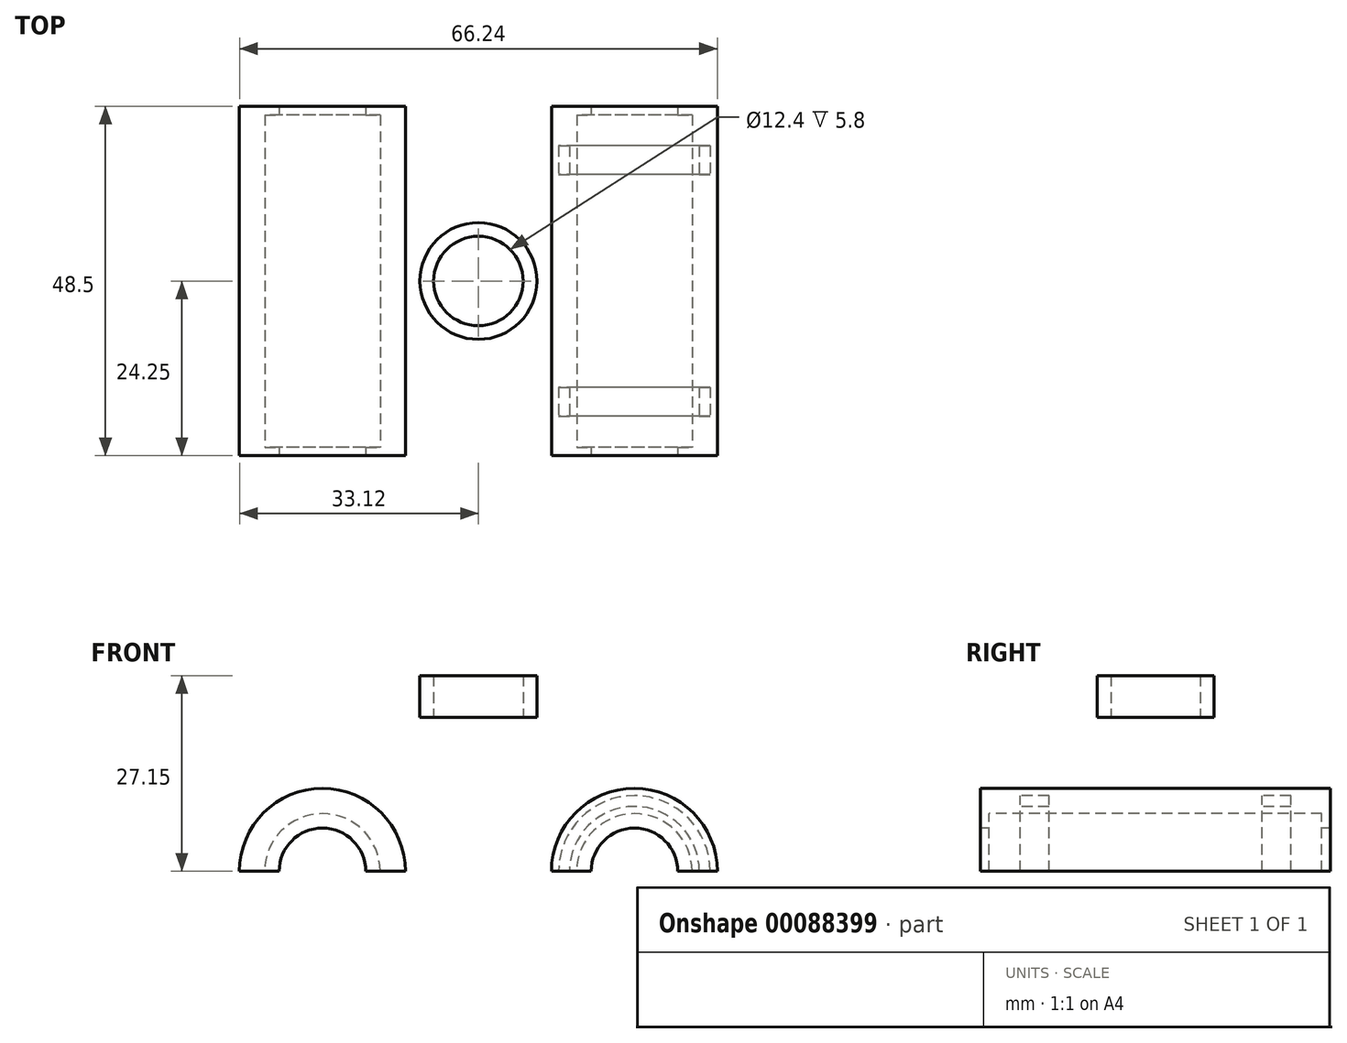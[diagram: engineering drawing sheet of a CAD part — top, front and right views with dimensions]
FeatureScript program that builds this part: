
annotation { "Feature Type Name" : "Feature", "Feature Type Description" : "" }
export const myFeature = defineFeature(function(context is Context, id is Id, definition is map)
    precondition{}
    {
        {
            var Q0;
            Q0=qCreatedBy(makeId("Front.planeOp"),FACE);
            var sketch = newSketch(context, id + "F0", { "sketchPlane" : qUnion([Q0])});
            skLineSegment(sketch, "E0", {"start": v(-21.63, 0) * mm, "end": v(21.63, 0) * mm, "construction": true});
            skCircle(sketch, "E1", {"center": v(-21.63, 0) * mm, "radius": 8 * mm});
            skCircle(sketch, "E2", {"center": v(21.63, 0) * mm, "radius": 8 * mm});
            skCircle(sketch, "E3", {"center": v(-21.63, 0) * mm, "radius": 6 * mm});
            skCircle(sketch, "E4", {"center": v(21.63, 0) * mm, "radius": 6 * mm});
            skCircle(sketch, "E5", {"center": v(-21.63, 0) * mm, "radius": 11.5 * mm});
            skCircle(sketch, "E6", {"center": v(21.63, 0) * mm, "radius": 11.5 * mm});
            skLineSegment(sketch, "E7", {"start": v(-33.12, 0) * mm, "end": v(33.12, 0) * mm});
            skSolve(sketch);
        }
        {
            var Q0;
            {var subQ0=sQuery(id+"F0.wireOp",EDGE,"E7");var subQ1=sQuery(id+"F0.wireOp",EDGE,"E1");var subQ2=makeQuery(id+"F0.imprint","INTERSECT",VERTEX,{"disambiguationData":[OD(0.0)],"derivedFrom":[subQ1,subQ0]});Q0=makeQuery(id+"F0.imprint","IMPRINT",FACE,{"disambiguationData":[TD([[makeQuery(id+"F0.imprint","IMPRINT",EDGE,{"disambiguationData":[TD([[subQ2,1.0]])],"derivedFrom":subQ1}),1.0]])]});}
            var Q1;
            {var subQ0=sQuery(id+"F0.wireOp",EDGE,"E7");var subQ1=sQuery(id+"F0.wireOp",EDGE,"E1");var subQ2=makeQuery(id+"F0.imprint","INTERSECT",VERTEX,{"disambiguationData":[OD(0.0)],"derivedFrom":[subQ1,subQ0]});Q1=makeQuery(id+"F0.imprint","IMPRINT",FACE,{"disambiguationData":[TD([[makeQuery(id+"F0.imprint","IMPRINT",EDGE,{"disambiguationData":[TD([[subQ2,1.0]])],"derivedFrom":subQ1}),-1.0]])]});}
            var Q2;
            {var subQ0=sQuery(id+"F0.wireOp",EDGE,"E7");var subQ1=sQuery(id+"F0.wireOp",EDGE,"E2");var subQ2=makeQuery(id+"F0.imprint","INTERSECT",VERTEX,{"disambiguationData":[OD(0.0)],"derivedFrom":[subQ1,subQ0]});Q2=makeQuery(id+"F0.imprint","IMPRINT",FACE,{"disambiguationData":[TD([[makeQuery(id+"F0.imprint","IMPRINT",EDGE,{"disambiguationData":[TD([[subQ2,1.0]])],"derivedFrom":subQ1}),1.0]])]});}
            var Q3;
            {var subQ0=sQuery(id+"F0.wireOp",EDGE,"E7");var subQ1=sQuery(id+"F0.wireOp",EDGE,"E2");var subQ2=makeQuery(id+"F0.imprint","INTERSECT",VERTEX,{"disambiguationData":[OD(0.0)],"derivedFrom":[subQ1,subQ0]});Q3=makeQuery(id+"F0.imprint","IMPRINT",FACE,{"disambiguationData":[TD([[makeQuery(id+"F0.imprint","IMPRINT",EDGE,{"disambiguationData":[TD([[subQ2,1.0]])],"derivedFrom":subQ1}),-1.0]])]});}
            extrude(context, id + "F1", {"entities" : qUnion([Q0, Q1, Q2, Q3]), "oppositeDirection" : true, "depth" : 48.5 * mm});
        }
        {
            var Q0;
            {var subQ0=sQuery(id+"F0.wireOp",EDGE,"E7");var subQ1=sQuery(id+"F0.wireOp",EDGE,"E1");var subQ2=makeQuery(id+"F0.imprint","INTERSECT",VERTEX,{"disambiguationData":[OD(0.0)],"derivedFrom":[subQ1,subQ0]});Q0=makeQuery(id+"F0.imprint","IMPRINT",FACE,{"disambiguationData":[TD([[makeQuery(id+"F0.imprint","IMPRINT",EDGE,{"disambiguationData":[TD([[subQ2,1.0]])],"derivedFrom":subQ1}),1.0]])]});}
            var Q1;
            {var subQ0=sQuery(id+"F0.wireOp",EDGE,"E7");var subQ1=sQuery(id+"F0.wireOp",EDGE,"E2");var subQ2=makeQuery(id+"F0.imprint","INTERSECT",VERTEX,{"disambiguationData":[OD(0.0)],"derivedFrom":[subQ1,subQ0]});Q1=makeQuery(id+"F0.imprint","IMPRINT",FACE,{"disambiguationData":[TD([[makeQuery(id+"F0.imprint","IMPRINT",EDGE,{"disambiguationData":[TD([[subQ2,1.0]])],"derivedFrom":subQ1}),1.0]])]});}
            extrude(context, id + "F2", {"entities" : qUnion([Q0, Q1]), "operationType" : NewBodyOperationType.REMOVE, "oppositeDirection" : true, "depth" : 47.3 * mm, "hasSecondDirection" : true, "secondDirectionOppositeDirection" : true, "secondDirectionDepth" : 1.2 * mm});
        }
        {
            var Q0;
            Q0=qCreatedBy(makeId("Front.planeOp"),FACE);
            var sketch = newSketch(context, id + "F3", { "sketchPlane" : qUnion([Q0])});
            skPoint(sketch, "E8.0", {"position": v(-21.63, 0) * mm});
            skPoint(sketch, "E9.0", {"position": v(21.63, 0) * mm});
            skLineSegment(sketch, "E10.0", {"start": v(-33.12, 0) * mm, "end": v(33.12, 0) * mm});
            skCircle(sketch, "E11", {"center": v(-21.63, 0) * mm, "radius": 9 * mm});
            skCircle(sketch, "E12", {"center": v(-21.63, 0) * mm, "radius": 10.5 * mm});
            skCircle(sketch, "E13", {"center": v(21.63, 0) * mm, "radius": 9 * mm});
            skCircle(sketch, "E14", {"center": v(21.63, 0) * mm, "radius": 10.5 * mm});
            skSolve(sketch);
        }
        {
            var Q0;
            {var subQ0=sQuery(id+"F3.wireOp",EDGE,"E12");var subQ1=sQuery(id+"F3.wireOp",EDGE,"E10.0");var subQ2=makeQuery(id+"F3.imprint","INTERSECT",VERTEX,{"disambiguationData":[OD(0.0)],"derivedFrom":[subQ1,subQ0]});Q0=makeQuery(id+"F3.imprint","IMPRINT",FACE,{"disambiguationData":[TD([[makeQuery(id+"F3.imprint","IMPRINT",EDGE,{"disambiguationData":[TD([[subQ2,-1.0]])],"derivedFrom":subQ1}),1.0]])]});}
            var Q1;
            {var subQ0=sQuery(id+"F3.wireOp",EDGE,"E14");var subQ1=sQuery(id+"F3.wireOp",EDGE,"E10.0");var subQ2=makeQuery(id+"F3.imprint","INTERSECT",VERTEX,{"disambiguationData":[OD(0.0)],"derivedFrom":[subQ1,subQ0]});Q1=makeQuery(id+"F3.imprint","IMPRINT",FACE,{"disambiguationData":[TD([[makeQuery(id+"F3.imprint","IMPRINT",EDGE,{"disambiguationData":[TD([[subQ2,-1.0]])],"derivedFrom":subQ1}),1.0]])]});}
            extrude(context, id + "F4", {"entities" : qUnion([Q0, Q1]), "operationType" : NewBodyOperationType.REMOVE, "oppositeDirection" : true, "depth" : 9.5 * mm, "hasSecondDirection" : true, "secondDirectionOppositeDirection" : true, "secondDirectionDepth" : 5.5 * mm});
        }
        {
            var Q0;
            {var subQ0=sQuery(id+"F3.wireOp",EDGE,"E12");var subQ1=sQuery(id+"F3.wireOp",EDGE,"E10.0");var subQ2=makeQuery(id+"F3.imprint","INTERSECT",VERTEX,{"disambiguationData":[OD(0.0)],"derivedFrom":[subQ1,subQ0]});Q0=makeQuery(id+"F3.imprint","IMPRINT",FACE,{"disambiguationData":[TD([[makeQuery(id+"F3.imprint","IMPRINT",EDGE,{"disambiguationData":[TD([[subQ2,-1.0]])],"derivedFrom":subQ1}),1.0]])]});}
            var Q1;
            {var subQ0=sQuery(id+"F3.wireOp",EDGE,"E14");var subQ1=sQuery(id+"F3.wireOp",EDGE,"E10.0");var subQ2=makeQuery(id+"F3.imprint","INTERSECT",VERTEX,{"disambiguationData":[OD(0.0)],"derivedFrom":[subQ1,subQ0]});Q1=makeQuery(id+"F3.imprint","IMPRINT",FACE,{"disambiguationData":[TD([[makeQuery(id+"F3.imprint","IMPRINT",EDGE,{"disambiguationData":[TD([[subQ2,-1.0]])],"derivedFrom":subQ1}),1.0]])]});}
            extrude(context, id + "F5", {"entities" : qUnion([Q0, Q1]), "operationType" : NewBodyOperationType.REMOVE, "oppositeDirection" : true, "depth" : 43 * mm, "hasSecondDirection" : true, "secondDirectionOppositeDirection" : true, "secondDirectionDepth" : 39 * mm});
        }
        {
            var Q0;
            Q0=qCreatedBy(makeId("Top.planeOp"),FACE);
            var sketch = newSketch(context, id + "F6", { "sketchPlane" : qUnion([Q0])});
            skLineSegment(sketch, "E15.0", {"start": v(-10.13, 48.5) * mm, "end": v(-33.12, 48.5) * mm, "construction": true});
            skLineSegment(sketch, "E16.0", {"start": v(33.12, 48.5) * mm, "end": v(10.13, 48.5) * mm, "construction": true});
            skLineSegment(sketch, "E17", {"start": v(-10.13, 48.5) * mm, "end": v(10.13, 48.5) * mm, "construction": true});
            skLineSegment(sketch, "E18", {"start": v(0, 0) * mm, "end": v(0, 48.5) * mm, "construction": true});
            skCircle(sketch, "E19", {"center": v(0, 24.25) * mm, "radius": 6.2 * mm});
            skCircle(sketch, "E20", {"center": v(0, 24.25) * mm, "radius": 8.1 * mm});
            skSolve(sketch);
        }
        {
            var Q0;
            Q0=makeQuery(id+"F6.imprint","IMPRINT",FACE,{"disambiguationData":[TD([[makeQuery(id+"F6.imprint","IMPRINT",EDGE,{"derivedFrom":sQuery(id+"F6.wireOp",EDGE,"E19")}),-1.0]])]});
            extrude(context, id + "F7", {"entities" : qUnion([Q0]), "depth" : 27.15 * mm, "hasSecondDirection" : true, "secondDirectionOppositeDirection" : false, "secondDirectionDepth" : 21.35 * mm});
        }
    });
